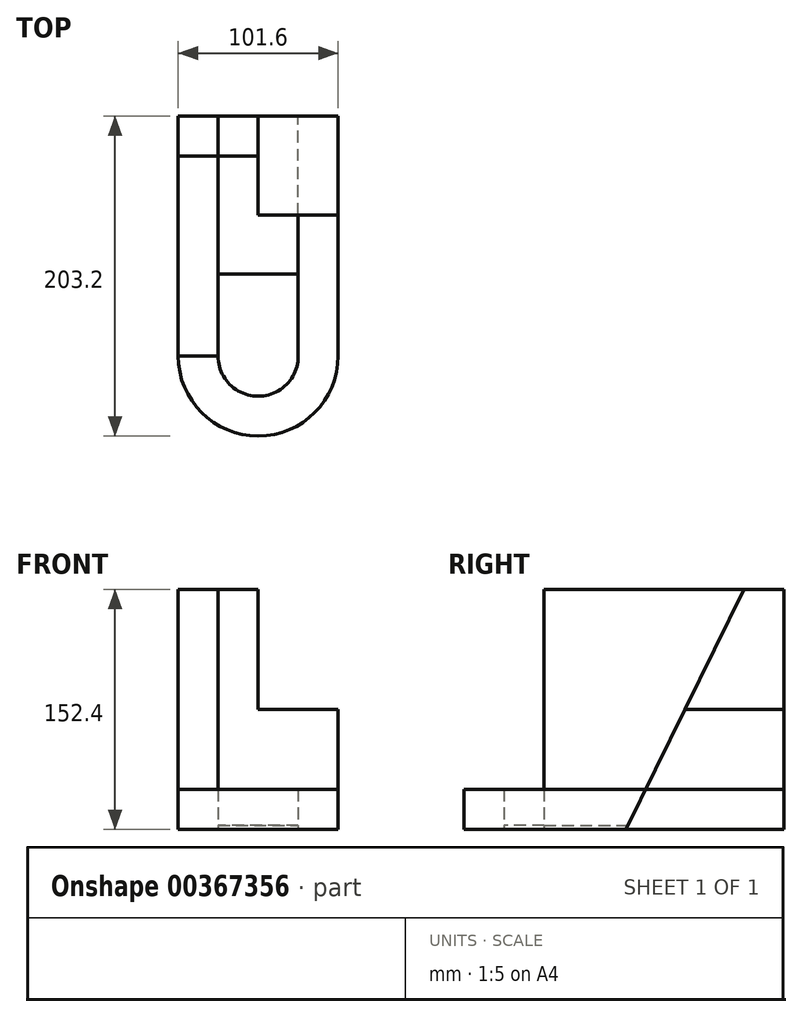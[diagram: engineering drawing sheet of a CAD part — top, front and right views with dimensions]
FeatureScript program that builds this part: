
annotation { "Feature Type Name" : "Feature", "Feature Type Description" : "" }
export const myFeature = defineFeature(function(context is Context, id is Id, definition is map)
    precondition{}
    {
        {
            var Q0;
            Q0=qCreatedBy(makeId("Top.planeOp"),FACE);
            var sketch = newSketch(context, id + "F0", { "sketchPlane" : qUnion([Q0])});
            skLineSegment(sketch, "E0.bottom", {"start": v(-67.56, 137.22) * mm, "end": v(34.04, 137.22) * mm});
            skLineSegment(sketch, "E0.left", {"start": v(-67.56, 137.22) * mm, "end": v(-67.56, -15.18) * mm});
            skLineSegment(sketch, "E0.right", {"start": v(34.04, 137.22) * mm, "end": v(34.04, -15.18) * mm});
            skArc(sketch, "E1", {"start": v(-67.56, -15.18) * mm, "mid": v(-16.76, -65.98) * mm, "end": v(34.04, -15.18) * mm});
            skLineSegment(sketch, "E2", {"start": v(-67.56, -15.18) * mm, "end": v(-42.16, -15.18) * mm});
            skLineSegment(sketch, "E3", {"start": v(34.04, -15.18) * mm, "end": v(8.64, -15.18) * mm});
            skArc(sketch, "E4", {"start": v(-42.16, -15.18) * mm, "mid": v(-16.76, -40.71) * mm, "end": v(8.64, -15.18) * mm});
            skLineSegment(sketch, "E5", {"start": v(-42.16, -15.18) * mm, "end": v(-42.16, 137.22) * mm});
            skLineSegment(sketch, "E6", {"start": v(8.64, -15.18) * mm, "end": v(8.64, 137.22) * mm});
            skLineSegment(sketch, "E7", {"start": v(-42.16, -15.18) * mm, "end": v(-42.16, 36.89) * mm});
            skLineSegment(sketch, "E8", {"start": v(-42.16, 36.89) * mm, "end": v(8.64, 36.89) * mm});
            skLineSegment(sketch, "E9", {"start": v(-67.56, 137.22) * mm, "end": v(-16.76, 137.22) * mm});
            skLineSegment(sketch, "E10", {"start": v(-16.76, 137.22) * mm, "end": v(-16.76, 111.82) * mm});
            skLineSegment(sketch, "E11", {"start": v(-16.76, 111.82) * mm, "end": v(-42.16, 111.82) * mm});
            skLineSegment(sketch, "E12", {"start": v(8.64, 137.22) * mm, "end": v(8.64, 36.89) * mm});
            skLineSegment(sketch, "E13", {"start": v(-42.16, 36.89) * mm, "end": v(-67.56, 36.89) * mm});
            skLineSegment(sketch, "E14", {"start": v(-67.56, 36.89) * mm, "end": v(34.04, 36.89) * mm});
            skLineSegment(sketch, "E15", {"start": v(34.04, 36.89) * mm, "end": v(8.64, 36.89) * mm});
            skLineSegment(sketch, "E16", {"start": v(-42.16, 44.15) * mm, "end": v(8.64, 44.15) * mm});
            skSolve(sketch);
        }
        {
            var Q0;
            {var subQ0=sQuery(id+"F0.wireOp",EDGE,"E4");Q0=makeQuery(id+"F0.imprint","IMPRINT",FACE,{"disambiguationData":[TD([[makeQuery(id+"F0.imprint","IMPRINT",EDGE,{"derivedFrom":subQ0}),1.0]])]});}
            var Q1;
            {var subQ2=sQuery(id+"F0.wireOp",EDGE,"E8");Q1=makeQuery(id+"F0.imprint","IMPRINT",FACE,{"disambiguationData":[TD([[makeQuery(id+"F0.imprint","IMPRINT",EDGE,{"derivedFrom":subQ2}),1.0]])]});}
            extrude(context, id + "F1", {"entities" : qUnion([Q0, Q1]), "depth" : 2.54 * mm});
        }
        {
            var Q0;
            {var subQ2=sQuery(id+"F0.wireOp",EDGE,"E14");Q0=makeQuery(id+"F0.imprint","IMPRINT",FACE,{"disambiguationData":[TD([[makeQuery(id+"F0.imprint","IMPRINT",EDGE,{"derivedFrom":subQ2}),1.0]])]});}
            var Q1;
            {var subQ6=sQuery(id+"F0.wireOp",EDGE,"E10");Q1=makeQuery(id+"F0.imprint","IMPRINT",FACE,{"disambiguationData":[TD([[makeQuery(id+"F0.imprint","IMPRINT",EDGE,{"derivedFrom":subQ6}),1.0]])]});}
            var Q2;
            {var subQ0=sQuery(id+"F0.wireOp",EDGE,"E10");Q2=makeQuery(id+"F0.imprint","IMPRINT",FACE,{"disambiguationData":[TD([[makeQuery(id+"F0.imprint","IMPRINT",EDGE,{"derivedFrom":subQ0}),-1.0]])]});}
            var Q3;
            {var subQ7=sQuery(id+"F0.wireOp",EDGE,"E13");Q3=makeQuery(id+"F0.imprint","IMPRINT",FACE,{"disambiguationData":[TD([[makeQuery(id+"F0.imprint","IMPRINT",EDGE,{"derivedFrom":subQ7}),-1.0]])]});}
            var Q4;
            {var subQ2=sQuery(id+"F0.wireOp",EDGE,"E8");Q4=makeQuery(id+"F0.imprint","IMPRINT",FACE,{"disambiguationData":[TD([[makeQuery(id+"F0.imprint","IMPRINT",EDGE,{"derivedFrom":subQ2}),1.0]])]});}
            extrude(context, id + "F2", {"entities" : qUnion([Q0, Q1, Q2, Q3, Q4]), "operationType" : NewBodyOperationType.ADD, "depth" : 152.4 * mm});
        }
        {
            var Q0;
            Q0=makeQuery(id+"F2.opExtrude","SWEPT_FACE",FACE,{"disambiguationData":[OSD([sQuery(id+"F0.wireOp",EDGE,"E0.right")])]});
            var sketch = newSketch(context, id + "F3", { "sketchPlane" : qUnion([Q0])});
            skLineSegment(sketch, "E17", {"start": v(137.22, 152.4) * mm, "end": v(111.82, 152.4) * mm});
            skLineSegment(sketch, "E18", {"start": v(111.82, 152.4) * mm, "end": v(36.89, 0) * mm});
            skLineSegment(sketch, "E19", {"start": v(36.89, 0) * mm, "end": v(36.89, 152.4) * mm});
            skLineSegment(sketch, "E20", {"start": v(36.89, 152.4) * mm, "end": v(111.82, 152.4) * mm});
            skSolve(sketch);
        }
        {
            var Q0;
            Q0=makeQuery(id+"F3.imprint","IMPRINT",FACE,{"disambiguationData":[TD([[makeQuery(id+"F3.imprint","IMPRINT",EDGE,{"derivedFrom":sQuery(id+"F3.wireOp",EDGE,"E18")}),-1.0]])]});
            extrude(context, id + "F4", {"entities" : qUnion([Q0]), "operationType" : NewBodyOperationType.REMOVE, "oppositeDirection" : true, "depth" : 101.6 * mm});
        }
        {
            var Q0;
            Q0=makeQuery(id+"F2.opExtrude","SWEPT_FACE",FACE,{"disambiguationData":[OSD([sQuery(id+"F0.wireOp",EDGE,"E0.bottom")])]});
            var sketch = newSketch(context, id + "F5", { "sketchPlane" : qUnion([Q0])});
            skLineSegment(sketch, "E21", {"start": v(-34.04, 152.4) * mm, "end": v(16.76, 152.4) * mm});
            skLineSegment(sketch, "E22", {"start": v(16.76, 152.4) * mm, "end": v(16.76, 76.2) * mm});
            skLineSegment(sketch, "E23", {"start": v(16.76, 76.2) * mm, "end": v(-34.04, 76.2) * mm});
            skSolve(sketch);
        }
        {
            var Q0;
            Q0 = qSketchRegion(id + "F5", true);
            var Q1;
            {var subQ0=sQuery(id+"F5.wireOp",EDGE,"E21");Q1=makeQuery(id+"F5.imprint","IMPRINT",FACE,{"disambiguationData":[TD([[makeQuery(id+"F5.imprint","IMPRINT",EDGE,{"derivedFrom":subQ0}),1.0]])]});}
            extrude(context, id + "F6", {"entities" : qUnion([Q0, Q1]), "operationType" : NewBodyOperationType.REMOVE, "oppositeDirection" : true, "depth" : 63.5 * mm});
        }
        {
            var Q0;
            {var subQ0=sQuery(id+"F0.wireOp",EDGE,"E2");Q0=makeQuery(id+"F0.imprint","IMPRINT",FACE,{"disambiguationData":[TD([[makeQuery(id+"F0.imprint","IMPRINT",EDGE,{"derivedFrom":subQ0}),1.0]])]});}
            var Q1;
            {var subQ7=sQuery(id+"F0.wireOp",EDGE,"E13");Q1=makeQuery(id+"F0.imprint","IMPRINT",FACE,{"disambiguationData":[TD([[makeQuery(id+"F0.imprint","IMPRINT",EDGE,{"derivedFrom":subQ7}),-1.0]])]});}
            extrude(context, id + "F7", {"entities" : qUnion([Q0, Q1]), "depth" : 152.4 * mm});
        }
        {
            var Q0;
            Q0=makeQuery(id+"F0.imprint","IMPRINT",FACE,{"disambiguationData":[TD([[makeQuery(id+"F0.imprint","IMPRINT",EDGE,{"derivedFrom":sQuery(id+"F0.wireOp",EDGE,"E1")}),1.0]])]});
            var Q1;
            {var subQ0=sQuery(id+"F0.wireOp",EDGE,"E3");Q1=makeQuery(id+"F0.imprint","IMPRINT",FACE,{"disambiguationData":[TD([[makeQuery(id+"F0.imprint","IMPRINT",EDGE,{"derivedFrom":subQ0}),-1.0]])]});}
            var Q2;
            {var subQ2=sQuery(id+"F0.wireOp",EDGE,"E14");Q2=makeQuery(id+"F0.imprint","IMPRINT",FACE,{"disambiguationData":[TD([[makeQuery(id+"F0.imprint","IMPRINT",EDGE,{"derivedFrom":subQ2}),1.0]])]});}
            extrude(context, id + "F8", {"entities" : qUnion([Q0, Q1, Q2]), "depth" : 25.4 * mm});
        }
    });
